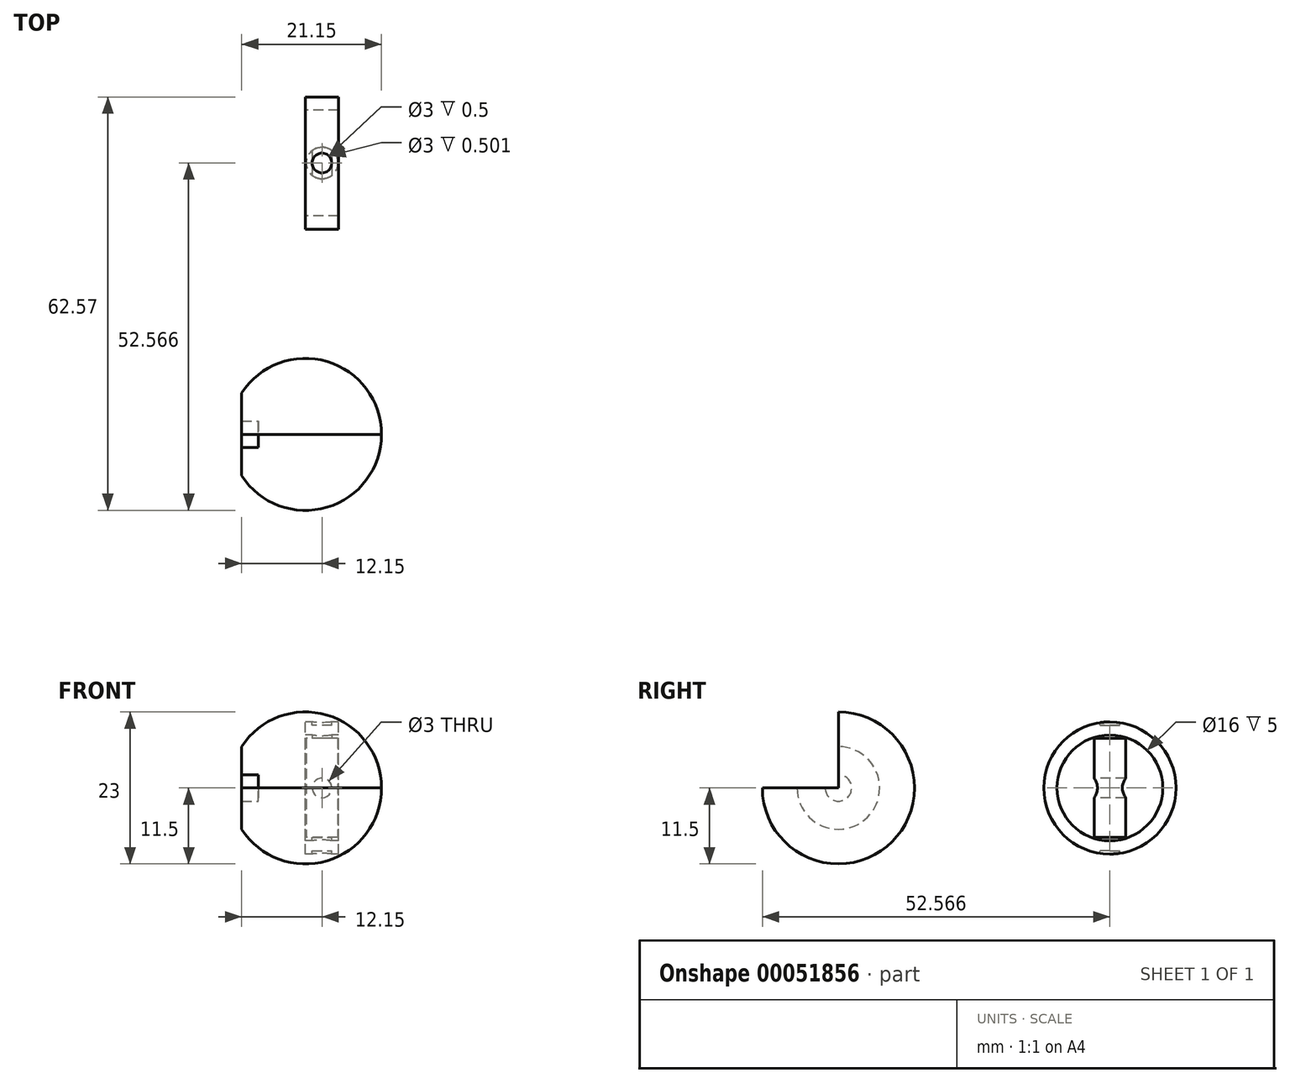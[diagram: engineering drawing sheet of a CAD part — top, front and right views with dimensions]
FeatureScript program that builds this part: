
annotation { "Feature Type Name" : "Feature", "Feature Type Description" : "" }
export const myFeature = defineFeature(function(context is Context, id is Id, definition is map)
    precondition{}
    {
        {
            var Q0;
            Q0=qCreatedBy(makeId("Front.planeOp"),FACE);
            var sketch = newSketch(context, id + "F0", { "sketchPlane" : qUnion([Q0])});
            skArc(sketch, "E0", {"start": v(13, 0) * mm, "mid": v(3.07, 12.63) * mm, "end": v(-11.55, 5.98) * mm});
            skArc(sketch, "E1", {"start": v(-11.55, 5.98) * mm, "mid": v(-13.36, 3.23) * mm, "end": v(-14, 0) * mm});
            skLineSegment(sketch, "E2", {"start": v(-14, 0) * mm, "end": v(-13, 0) * mm});
            skPoint(sketch, "E3.orphan", {"position": v(-18.44, 0) * mm});
            skSolve(sketch);
        }
        {
            var Q0;
            Q0=qCreatedBy(makeId("Front.planeOp"),FACE);
            var sketch = newSketch(context, id + "F1", { "sketchPlane" : qUnion([Q0])});
            skLineSegment(sketch, "E4", {"start": v(-17.79, 0) * mm, "end": v(17.77, 0) * mm});
            skSolve(sketch);
        }
        {
            var Q0;
            {var subQ0=sQuery(id+"F0.wireOp",EDGE,"E2");var subQ1=sQuery(id+"F0.wireOp",EDGE,"E0");var subQ2=makeQuery(id+"F0.imprint","INTERSECT",VERTEX,{"disambiguationData":[OD(0.0)],"derivedFrom":[subQ1,subQ0]});Q0=makeQuery(id+"F0.imprint","IMPRINT",FACE,{"disambiguationData":[TD([[makeQuery(id+"F0.imprint","IMPRINT",EDGE,{"disambiguationData":[TD([[subQ2,-1.0]])],"derivedFrom":subQ1}),1.0]])]});}
            var Q1;
            {var subQ0=sQuery(id+"F0.wireOp",EDGE,"E2");var subQ1=sQuery(id+"F0.wireOp",EDGE,"E0");var subQ2=makeQuery(id+"F0.imprint","INTERSECT",VERTEX,{"disambiguationData":[OD(1.0)],"derivedFrom":[subQ1,subQ0]});Q1=makeQuery(id+"F0.imprint","IMPRINT",FACE,{"disambiguationData":[TD([[makeQuery(id+"F0.imprint","IMPRINT",EDGE,{"disambiguationData":[TD([[subQ2,1.0]])],"derivedFrom":subQ1}),-1.0]])]});}
            var Q2;
            Q2=sQuery(id+"F0.wireOp",EDGE,"E0");
            var Q3;
            Q3=sQuery(id+"F0.wireOp",EDGE,"E1");
            var Q4;
            Q4=sQuery(id+"F0.wireOp",EDGE,"E2");
            revolve(context, id + "F2", {"bodyType" : ToolBodyType.SURFACE, "entities" : qUnion([Q0, Q1]), "surfaceEntities" : qUnion([Q2, Q3]), "axis" : qUnion([Q4]), "revolveType" : RevolveType.ONE_DIRECTION, "oppositeDirection" : true, "angle" : 270 * degree});
        }
        {
            var Q0;
            Q0=qCreatedBy(makeId("Front.planeOp"),FACE);
            var sketch = newSketch(context, id + "F3", { "sketchPlane" : qUnion([Q0])});
            skArc(sketch, "E5", {"start": v(11.5, 0) * mm, "mid": v(3.26, 11.03) * mm, "end": v(-9.65, 6.25) * mm});
            skLineSegment(sketch, "E6", {"start": v(-9.65, 2) * mm, "end": v(-9.65, 6.25) * mm});
            skLineSegment(sketch, "E7", {"start": v(-9.65, 2) * mm, "end": v(-7.12, 2) * mm});
            skLineSegment(sketch, "E8", {"start": v(-7.12, 2) * mm, "end": v(-7.12, 0) * mm});
            skLineSegment(sketch, "E9", {"start": v(-7.12, 0) * mm, "end": v(11.5, 0) * mm});
            skSolve(sketch);
        }
        {
            var Q0;
            Q0=makeQuery(id+"F3.imprint","IMPRINT",FACE,{"disambiguationData":[TD([[makeQuery(id+"F3.imprint","IMPRINT",EDGE,{"derivedFrom":sQuery(id+"F3.wireOp",EDGE,"E5")}),1.0]])]});
            var Q1;
            Q1=sQuery(id+"F1.wireOp",EDGE,"E4");
            revolve(context, id + "F4", {"entities" : qUnion([Q0]), "axis" : qUnion([Q1]), "revolveType" : RevolveType.ONE_DIRECTION, "oppositeDirection" : true, "angle" : 270 * degree});
        }
        {
            var Q0;
            Q0=qCreatedBy(makeId("Right.planeOp"),FACE);
            var sketch = newSketch(context, id + "F5", { "sketchPlane" : qUnion([Q0])});
            skCircle(sketch, "E10", {"center": v(41.07, 0) * mm, "radius": 10 * mm});
            skCircle(sketch, "E11", {"center": v(41.07, 0) * mm, "radius": 8 * mm});
            skSolve(sketch);
        }
        {
            var Q0;
            Q0=makeQuery(id+"F5.imprint","IMPRINT",FACE,{"disambiguationData":[TD([[makeQuery(id+"F5.imprint","IMPRINT",EDGE,{"derivedFrom":sQuery(id+"F5.wireOp",EDGE,"E10")}),1.0]])]});
            extrude(context, id + "F6", {"entities" : qUnion([Q0]), "depth" : 5 * mm});
        }
        {
            var Q0;
            Q0=qCreatedBy(makeId("Top.planeOp"),FACE);
            var sketch = newSketch(context, id + "F7", { "sketchPlane" : qUnion([Q0])});
            skLineSegment(sketch, "E12", {"start": v(0, 41.07) * mm, "end": v(2.5, 41.07) * mm});
            skCircle(sketch, "E13", {"center": v(2.5, 41.07) * mm, "radius": 1.5 * mm});
            skCircle(sketch, "E14", {"center": v(2.5, 41.07) * mm, "radius": 2.4 * mm});
            skSolve(sketch);
        }
        {
            var Q0;
            Q0=makeQuery(id+"F7.imprint","IMPRINT",FACE,{"disambiguationData":[TD([[makeQuery(id+"F7.imprint","IMPRINT",EDGE,{"derivedFrom":sQuery(id+"F7.wireOp",EDGE,"E13")}),1.0]])]});
            extrude(context, id + "F8", {"entities" : qUnion([Q0]), "operationType" : NewBodyOperationType.REMOVE, "oppositeDirection" : true, "depth" : 11 * mm, "hasSecondDirection" : true, "secondDirectionOppositeDirection" : false, "secondDirectionDepth" : 25 * mm});
        }
        {
            var Q0;
            Q0=sQuery(id+"F7.wireOp",EDGE,"E12");
            extrude(context, id + "F9", {"bodyType" : ToolBodyType.SURFACE, "surfaceEntities" : qUnion([Q0]), "depth" : 2 * mm});
        }
        {
            var Q0;
            Q0=makeQuery(id+"F9.opExtrude","SWEPT_FACE",FACE,{"disambiguationData":[OSD([sQuery(id+"F7.wireOp",EDGE,"E12")])]});
            var sketch = newSketch(context, id + "F10", { "sketchPlane" : qUnion([Q0])});
            skCircle(sketch, "E15", {"center": v(2.5, 0) * mm, "radius": 1.5 * mm});
            skSolve(sketch);
        }
        {
            var Q0;
            Q0=makeQuery(id+"F7.imprint","IMPRINT",FACE,{"disambiguationData":[TD([[makeQuery(id+"F7.imprint","IMPRINT",EDGE,{"derivedFrom":sQuery(id+"F7.wireOp",EDGE,"E13")}),-1.0]])]});
            var Q1;
            Q1=makeQuery(id+"F7.imprint","IMPRINT",FACE,{"disambiguationData":[TD([[makeQuery(id+"F7.imprint","IMPRINT",EDGE,{"derivedFrom":sQuery(id+"F7.wireOp",EDGE,"E13")}),1.0]])]});
            extrude(context, id + "F11", {"entities" : qUnion([Q0, Q1]), "depth" : 7.5 * mm, "hasSecondDirection" : true, "secondDirectionOppositeDirection" : true, "secondDirectionDepth" : 7.5 * mm});
        }
        {
            var Q0;
            {var subQ0=sQuery(id+"F10.wireOp",EDGE,"E15");var subQ1=makeQuery(id+"F9.opExtrude","SWEPT_EDGE",EDGE,{"disambiguationData":[OSD([sQuery(id+"F7.wireOp",VERTEX,"E12.end")])]});var subQ2=makeQuery(id+"F10.imprint","INTERSECT",VERTEX,{"derivedFrom":[subQ1,subQ0]});Q0=makeQuery(id+"F10.imprint","IMPRINT",FACE,{"disambiguationData":[TD([[makeQuery(id+"F10.imprint","IMPRINT",EDGE,{"disambiguationData":[TD([[subQ2,1.0]])],"derivedFrom":subQ0}),1.0]])]});}
            var Q1;
            {var subQ0=sQuery(id+"F10.wireOp",EDGE,"E15");var subQ1=makeQuery(id+"F9.opExtrude","SWEPT_EDGE",EDGE,{"disambiguationData":[OSD([sQuery(id+"F7.wireOp",VERTEX,"E12.end")])]});var subQ2=makeQuery(id+"F10.imprint","INTERSECT",VERTEX,{"derivedFrom":[subQ1,subQ0]});Q1=makeQuery(id+"F10.imprint","IMPRINT",FACE,{"disambiguationData":[TD([[makeQuery(id+"F10.imprint","IMPRINT",EDGE,{"disambiguationData":[TD([[subQ2,-1.0]])],"derivedFrom":subQ0}),1.0]])]});}
            extrude(context, id + "F12", {"entities" : qUnion([Q0, Q1]), "operationType" : NewBodyOperationType.REMOVE, "oppositeDirection" : true, "depth" : 4 * mm, "hasSecondDirection" : true, "secondDirectionOppositeDirection" : false, "secondDirectionDepth" : 4 * mm});
        }
        {
            var Q0;
            Q0=makeQuery(id+"F11.opExtrude","CAP_FACE",FACE,{"disambiguationData":[OSD([sQuery(id+"F7.wireOp",EDGE,"E14")])],"isStart":false});
            var sketch = newSketch(context, id + "F13", { "sketchPlane" : qUnion([Q0])});
            skCircle(sketch, "E16", {"center": v(2.5, 41.07) * mm, "radius": 1.5 * mm});
            skSolve(sketch);
        }
        {
            var Q0;
            Q0=makeQuery(id+"F13.imprint","IMPRINT",FACE,{"disambiguationData":[TD([[makeQuery(id+"F13.imprint","IMPRINT",EDGE,{"derivedFrom":sQuery(id+"F13.wireOp",EDGE,"E16")}),1.0]])]});
            extrude(context, id + "F14", {"entities" : qUnion([Q0]), "operationType" : NewBodyOperationType.ADD, "depth" : 2 * mm});
        }
        {
            var Q0;
            Q0=makeQuery(id+"F11.opExtrude","CAP_FACE",FACE,{"disambiguationData":[OSD([sQuery(id+"F7.wireOp",EDGE,"E14")])],"isStart":true});
            var sketch = newSketch(context, id + "F15", { "sketchPlane" : qUnion([Q0])});
            skCircle(sketch, "E17", {"center": v(2.5, -41.07) * mm, "radius": 1.5 * mm});
            skSolve(sketch);
        }
        {
            var Q0;
            Q0=makeQuery(id+"F15.imprint","IMPRINT",FACE,{"disambiguationData":[TD([[makeQuery(id+"F15.imprint","IMPRINT",EDGE,{"derivedFrom":sQuery(id+"F15.wireOp",EDGE,"E17")}),1.0]])]});
            extrude(context, id + "F16", {"entities" : qUnion([Q0]), "operationType" : NewBodyOperationType.ADD, "depth" : 2 * mm});
        }
    });
